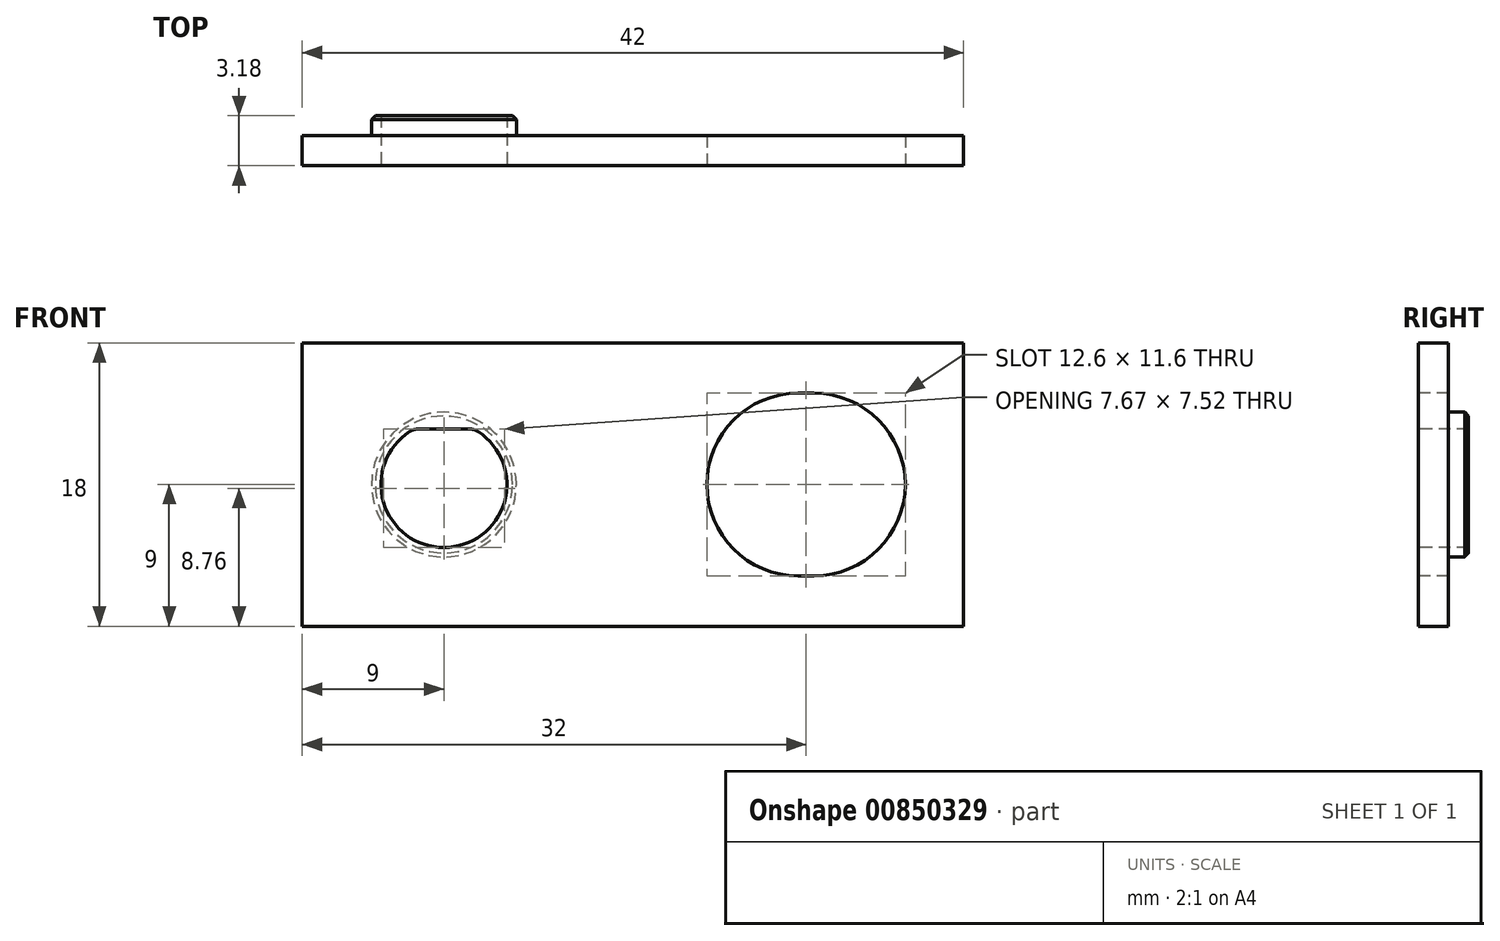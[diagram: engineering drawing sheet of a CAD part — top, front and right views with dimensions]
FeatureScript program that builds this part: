
annotation { "Feature Type Name" : "Feature", "Feature Type Description" : "" }
export const myFeature = defineFeature(function(context is Context, id is Id, definition is map)
    precondition{}
    {
        {
            var Q0;
            Q0=qCreatedBy(makeId("Front.planeOp"),FACE);
            var sketch = newSketch(context, id + "F0", { "sketchPlane" : qUnion([Q0])});
            skLineSegment(sketch, "E0.bottom", {"start": v(0, 0) * mm, "end": v(42, 0) * mm});
            skLineSegment(sketch, "E0.top", {"start": v(0, 18) * mm, "end": v(42, 18) * mm});
            skLineSegment(sketch, "E0.left", {"start": v(0, 0) * mm, "end": v(0, 18) * mm});
            skLineSegment(sketch, "E0.right", {"start": v(42, 0) * mm, "end": v(42, 18) * mm});
            skLineSegment(sketch, "E1.bottom", {"start": v(31.5, 3.2) * mm, "end": v(32.5, 3.2) * mm});
            skLineSegment(sketch, "E1.top", {"start": v(31.5, 14.8) * mm, "end": v(32.5, 14.8) * mm});
            skLineSegment(sketch, "E1.left", {"start": v(25.7, 9) * mm, "end": v(25.7, 9) * mm});
            skLineSegment(sketch, "E1.right", {"start": v(38.3, 9) * mm, "end": v(38.3, 9) * mm});
            skArc(sketch, "E2", {"start": v(6.83, 12.36) * mm, "mid": v(9, 5) * mm, "end": v(11.17, 12.36) * mm});
            skLineSegment(sketch, "E3", {"start": v(7.37, 12.52) * mm, "end": v(10.63, 12.52) * mm});
            skPoint(sketch, "E4.visualSharp", {"position": v(10.9, 12.52) * mm});
            skArc(sketch, "E4.filletArc", {"start": v(11.17, 12.36) * mm, "mid": v(10.91, 12.48) * mm, "end": v(10.63, 12.52) * mm});
            skPoint(sketch, "E5.visualSharp", {"position": v(7.1, 12.52) * mm});
            skArc(sketch, "E5.filletArc", {"start": v(7.37, 12.52) * mm, "mid": v(7.09, 12.48) * mm, "end": v(6.83, 12.36) * mm});
            skPoint(sketch, "E6.visualSharp", {"position": v(25.7, 14.8) * mm});
            skArc(sketch, "E6.filletArc", {"start": v(31.5, 14.8) * mm, "mid": v(27.4, 13.1) * mm, "end": v(25.7, 9) * mm});
            skPoint(sketch, "E7.visualSharp", {"position": v(25.7, 3.2) * mm});
            skArc(sketch, "E7.filletArc", {"start": v(25.7, 9) * mm, "mid": v(27.4, 4.9) * mm, "end": v(31.5, 3.2) * mm});
            skPoint(sketch, "E8.visualSharp", {"position": v(38.3, 3.2) * mm});
            skArc(sketch, "E8.filletArc", {"start": v(32.5, 3.2) * mm, "mid": v(36.6, 4.9) * mm, "end": v(38.3, 9) * mm});
            skPoint(sketch, "E9.visualSharp", {"position": v(38.3, 14.8) * mm});
            skArc(sketch, "E9.filletArc", {"start": v(38.3, 9) * mm, "mid": v(36.6, 13.1) * mm, "end": v(32.5, 14.8) * mm});
            skLineSegment(sketch, "E10", {"start": v(42, 9) * mm, "end": v(0, 9) * mm, "construction": true});
            skLineSegment(sketch, "E11", {"start": v(32, 14.8) * mm, "end": v(32, 3.2) * mm, "construction": true});
            skSolve(sketch);
        }
        {
            var Q0;
            Q0=makeQuery(id+"F0.imprint","IMPRINT",FACE,{"disambiguationData":[TD([[makeQuery(id+"F0.imprint","IMPRINT",EDGE,{"derivedFrom":sQuery(id+"F0.wireOp",EDGE,"E0.bottom")}),1.0]])]});
            var sketch = newSketch(context, id + "F1", { "sketchPlane" : qUnion([Q0])});
            skCircle(sketch, "E12", {"center": v(9, 9) * mm, "radius": 4.6 * mm});
            skSolve(sketch);
        }
        {
            var Q0;
            Q0=makeQuery(id+"F0.imprint","IMPRINT",FACE,{"disambiguationData":[TD([[makeQuery(id+"F0.imprint","IMPRINT",EDGE,{"derivedFrom":sQuery(id+"F0.wireOp",EDGE,"E0.bottom")}),1.0]])]});
            var Q1;
            Q1=makeQuery(id+"F0.imprint","IMPRINT",FACE,{"disambiguationData":[TD([[makeQuery(id+"F0.imprint","IMPRINT",EDGE,{"derivedFrom":sQuery(id+"F0.wireOp",EDGE,"Tf1pBFFb-AJpi-rEh9-hHGZ-P9tz6k3wTr3f")}),1.0]])]});
            extrude(context, id + "F2", {"entities" : qUnion([Q0, Q1]), "oppositeDirection" : true, "depth" : 1.91 * mm, "offsetDistance" : 25 * mm});
        }
        {
            var Q0;
            Q0=makeQuery(id+"F1.imprint","IMPRINT",FACE,{"disambiguationData":[TD([[makeQuery(id+"F1.imprint","IMPRINT",EDGE,{"derivedFrom":sQuery(id+"F1.wireOp",EDGE,"E12")}),1.0]])]});
            extrude(context, id + "F3", {"entities" : qUnion([Q0]), "operationType" : NewBodyOperationType.ADD, "oppositeDirection" : true, "depth" : 3.18 * mm, "offsetDistance" : 25 * mm});
        }
        {
            var Q0;
            Q0=makeQuery(id+"F3.opExtrude","CAP_EDGE",EDGE,{"disambiguationData":[OSD([sQuery(id+"F1.wireOp",EDGE,"E12")])],"isStart":false});
            chamfer(context, id + "F4", {"entities" : qUnion([Q0]), "width" : 0.25 * mm, "tangentPropagation" : true});
        }
    });
